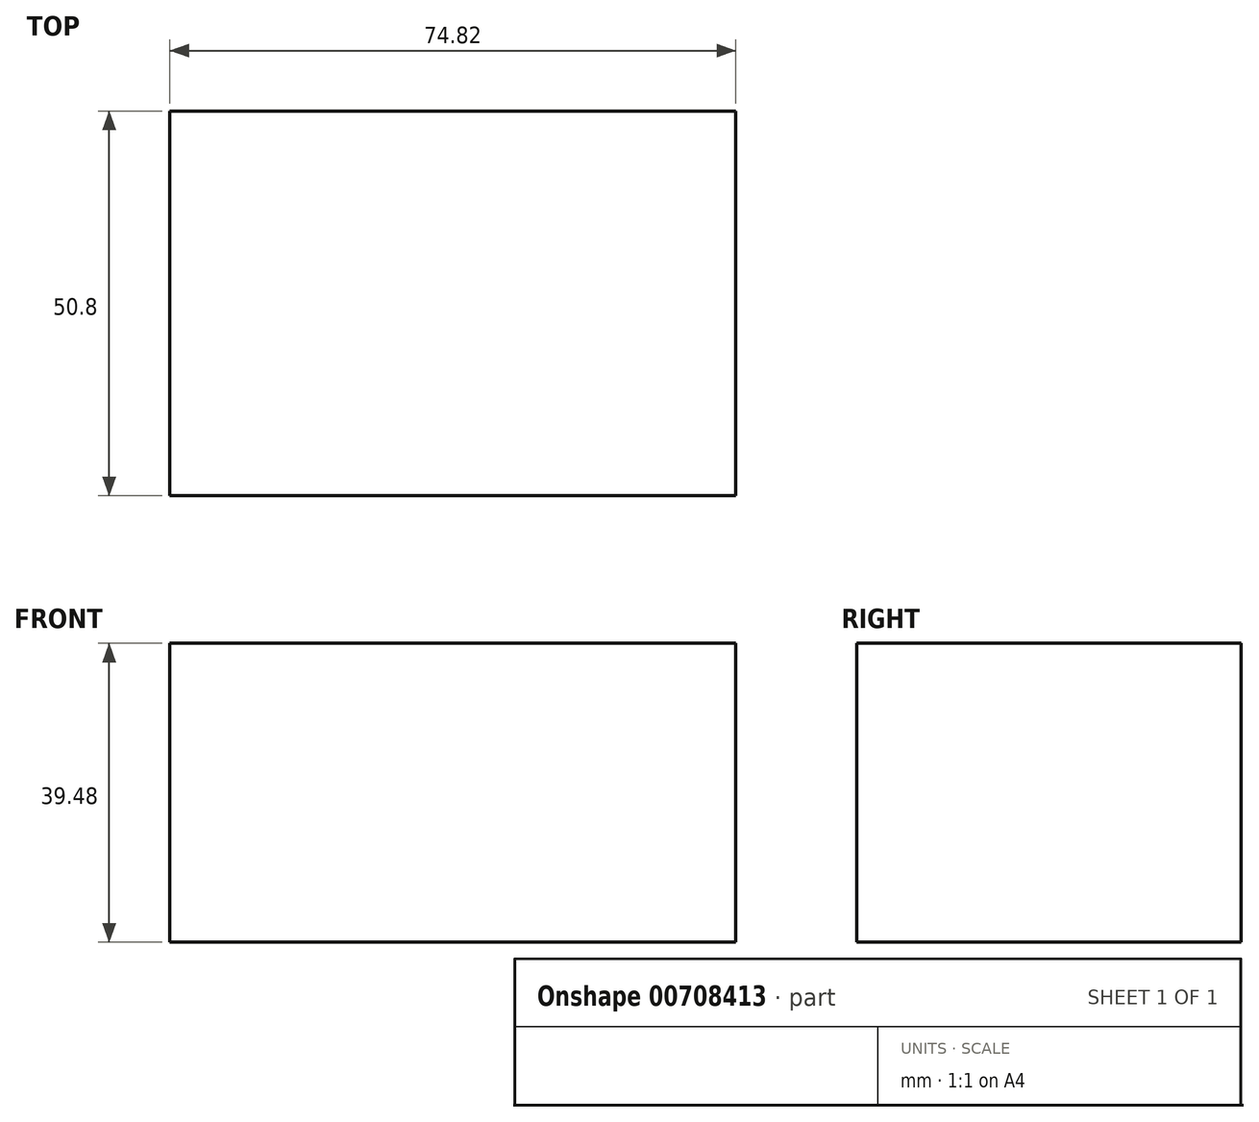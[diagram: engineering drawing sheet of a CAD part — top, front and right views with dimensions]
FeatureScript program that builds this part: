
annotation { "Feature Type Name" : "Feature", "Feature Type Description" : "" }
export const myFeature = defineFeature(function(context is Context, id is Id, definition is map)
    precondition{}
    {
        {
            var Q0;
            Q0=qCreatedBy(makeId("Front.planeOp"),FACE);
            var sketch = newSketch(context, id + "F0", { "sketchPlane" : qUnion([Q0])});
            skLineSegment(sketch, "E0.bottom", {"start": v(-45.81, 15.68) * mm, "end": v(29.01, 15.68) * mm});
            skLineSegment(sketch, "E0.top", {"start": v(-45.81, -23.8) * mm, "end": v(29.01, -23.8) * mm});
            skLineSegment(sketch, "E0.left", {"start": v(-45.81, 15.68) * mm, "end": v(-45.81, -23.8) * mm});
            skLineSegment(sketch, "E0.right", {"start": v(29.01, 15.68) * mm, "end": v(29.01, -23.8) * mm});
            skLineSegment(sketch, "E1.bottom", {"start": v(3.5, 68.79) * mm, "end": v(56.02, 68.79) * mm});
            skLineSegment(sketch, "E1.top", {"start": v(3.5, 34) * mm, "end": v(56.02, 34) * mm});
            skLineSegment(sketch, "E1.left", {"start": v(3.5, 68.79) * mm, "end": v(3.5, 34) * mm});
            skLineSegment(sketch, "E1.right", {"start": v(56.02, 68.79) * mm, "end": v(56.02, 34) * mm});
            skLineSegment(sketch, "E2", {"start": v(-45.81, 15.68) * mm, "end": v(-45.81, 53.65) * mm});
            skArc(sketch, "E3", {"start": v(3.5, 68.79) * mm, "mid": v(-24.77, 72.98) * mm, "end": v(-45.81, 53.65) * mm});
            skLineSegment(sketch, "E4", {"start": v(29.01, 15.68) * mm, "end": v(56.02, 34) * mm});
            skSolve(sketch);
        }
        {
            var Q0;
            Q0=makeQuery(id+"F0.imprint","IMPRINT",FACE,{"disambiguationData":[TD([[makeQuery(id+"F0.imprint","IMPRINT",EDGE,{"derivedFrom":sQuery(id+"F0.wireOp",EDGE,"E0.bottom")}),-1.0]])]});
            extrude(context, id + "F1", {"entities" : qUnion([Q0]), "depth" : 50.8 * mm, "offsetDistance" : 25.4 * mm});
        }
    });
